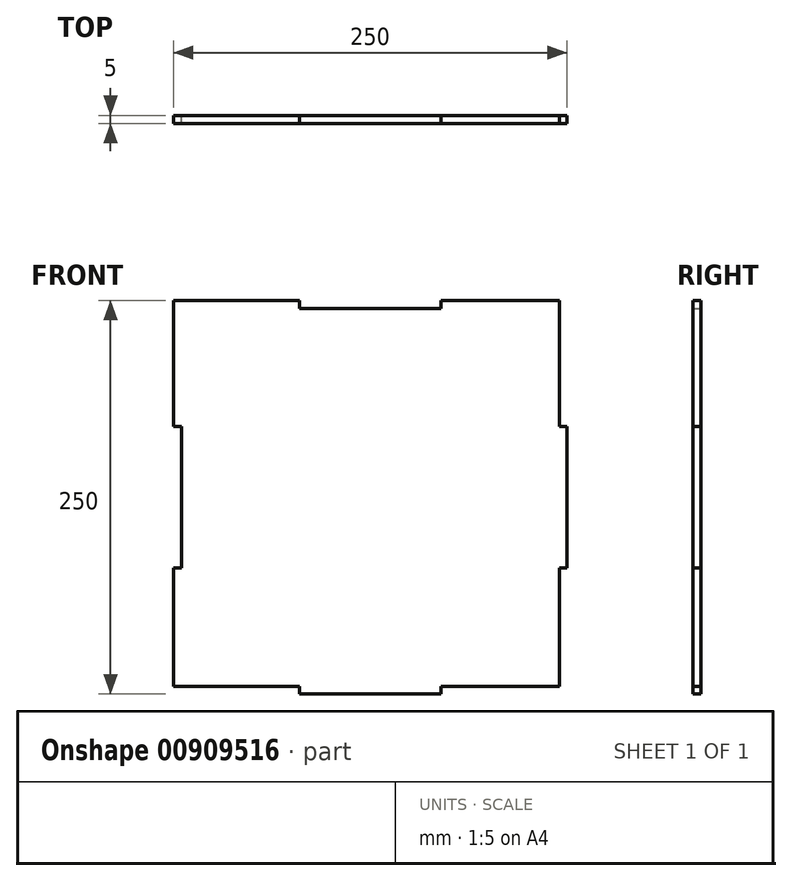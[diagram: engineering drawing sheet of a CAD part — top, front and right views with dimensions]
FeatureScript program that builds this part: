
annotation { "Feature Type Name" : "Feature", "Feature Type Description" : "" }
export const myFeature = defineFeature(function(context is Context, id is Id, definition is map)
    precondition{}
    {
        {
            var Q0;
            Q0=qCreatedBy(makeId("Front.planeOp"),FACE);
            var sketch = newSketch(context, id + "F0", { "sketchPlane" : qUnion([Q0])});
            skLineSegment(sketch, "E0.bottom", {"start": v(125, -125) * mm, "end": v(-125, -125) * mm});
            skLineSegment(sketch, "E0.top", {"start": v(125, 125) * mm, "end": v(-125, 125) * mm});
            skLineSegment(sketch, "E0.left", {"start": v(125, -125) * mm, "end": v(125, 125) * mm});
            skLineSegment(sketch, "E0.right", {"start": v(-125, -125) * mm, "end": v(-125, 125) * mm});
            skPoint(sketch, "E0.middle", {"position": v(0, 0) * mm});
            skSolve(sketch);
        }
        {
            var Q0;
            Q0=qCreatedBy(makeId("Front.planeOp"),FACE);
            var sketch = newSketch(context, id + "F1", { "sketchPlane" : qUnion([Q0])});
            skLineSegment(sketch, "E1.left", {"start": v(120, 120) * mm, "end": v(120, 45) * mm, "construction": true});
            skPoint(sketch, "E1.middle", {"position": v(0, 0) * mm});
            skLineSegment(sketch, "E2", {"start": v(0, 158) * mm, "end": v(0, -180.91) * mm, "construction": true});
            skPoint(sketch, "E2.endSnap0", {"position": v(0, -125) * mm});
            skLineSegment(sketch, "E3", {"start": v(-184.35, 0) * mm, "end": v(163.64, 0) * mm, "construction": true});
            skPoint(sketch, "E3.startSnap0", {"position": v(-125, 0) * mm});
            skLineSegment(sketch, "E4", {"start": v(-45, 125) * mm, "end": v(-45, 120) * mm});
            skLineSegment(sketch, "E5.MirrorCS", {"start": v(45, 125) * mm, "end": v(45, 120) * mm});
            skLineSegment(sketch, "E6.1.0", {"start": v(-125, 45) * mm, "end": v(-120, 45) * mm});
            skLineSegment(sketch, "E6.1.1", {"start": v(-125, -45) * mm, "end": v(-120, -45) * mm});
            skLineSegment(sketch, "E6.2.0", {"start": v(-45, -125) * mm, "end": v(-45, -120) * mm});
            skLineSegment(sketch, "E6.2.1", {"start": v(45, -125) * mm, "end": v(45, -120) * mm});
            skLineSegment(sketch, "E6.3.0", {"start": v(125, -45) * mm, "end": v(120, -45) * mm});
            skLineSegment(sketch, "E6.3.1", {"start": v(125, 45) * mm, "end": v(120, 45) * mm});
            skLineSegment(sketch, "E7", {"start": v(-45, 120) * mm, "end": v(45, 120) * mm});
            skLineSegment(sketch, "E8", {"start": v(-120, 45) * mm, "end": v(-120, -45) * mm});
            skLineSegment(sketch, "E9", {"start": v(120, -120) * mm, "end": v(45, -120) * mm});
            skLineSegment(sketch, "E10", {"start": v(120, -120) * mm, "end": v(120, -45) * mm});
            skLineSegment(sketch, "E11", {"start": v(-125, -120) * mm, "end": v(-125, -120) * mm});
            skLineSegment(sketch, "E12", {"start": v(120, 125) * mm, "end": v(45, 125) * mm});
            skLineSegment(sketch, "E13", {"start": v(-125, 45) * mm, "end": v(-125, 125) * mm});
            skLineSegment(sketch, "E14", {"start": v(-45, 125) * mm, "end": v(-125, 125) * mm});
            skLineSegment(sketch, "E15", {"start": v(-125, -120) * mm, "end": v(-125, -45) * mm});
            skLineSegment(sketch, "E16", {"start": v(-45, -120) * mm, "end": v(-125, -120) * mm});
            skLineSegment(sketch, "E17", {"start": v(120, 45) * mm, "end": v(120, 125) * mm});
            skLineSegment(sketch, "E18", {"start": v(125, 45) * mm, "end": v(125, -45) * mm});
            skLineSegment(sketch, "E19", {"start": v(45, -125) * mm, "end": v(-45, -125) * mm});
            skSolve(sketch);
        }
        {
            var Q0;
            Q0 = qSketchRegion(id + "F1", true);
            extrude(context, id + "F2", {"entities" : qUnion([Q0]), "depth" : 5 * mm, "offsetDistance" : 25.4 * mm});
        }
    });
